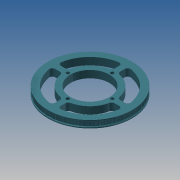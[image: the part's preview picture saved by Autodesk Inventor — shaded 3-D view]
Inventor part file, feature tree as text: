
AUTODESK INVENTOR PART (.ipt)
format: ipt  version: 2013 (Build 170138000, 138)  size: 1,232,896 bytes
history: native  units: mm
features: extrude x7, sketch x7, pattern_circular x3, mirror x1, chamfer x1, fillet x1
ambient origin geometry x8: Origin, YZ Plane, XZ Plane, XY Plane, X Axis, Y Axis, Z Axis, Center Point
bodies: Solid2 (feature_tree)
feature tree (20):
  extrude  "Extrusion11"  Depth=10.0mm
  extrude  "Extrusion12"  Depth=3.5mm
  pattern_circular  "Circular Pattern4"  Count=235  [1 undecoded]
  extrude  "Extrusion16"  Depth=1.0mm
  mirror  "Mirror2"
  chamfer  "Chamfer3"  Distance=2.5mm
  extrude  "Extrusion17"  Depth=1.0mm TaperAngle=45.0deg
  extrude  "Extrusion8"  Depth=12.0mm
  pattern_circular  "Circular Pattern5"  Count=7  [1 undecoded]
  fillet  "Fillet2"  Radius=10.0mm
  extrude  "Extrusion18"  Depth=2.5mm TaperAngle=0.0deg
  extrude  "Extrusion19"  Depth=40.0mm TaperAngle=360.0deg
  pattern_circular  "Circular Pattern6"  [2 undecoded]
  sketch  "Sketch8"  dims[d11=0.254mm d60=10.0mm]
  sketch  "Sketch9"  dims[d62=10.0mm d63=0.0mm d69=3.5mm]
  sketch  "Sketch11"  dims[d78=149.097647mm]
  sketch  "Sketch12"  dims[d80=8.0mm d81=0.0mm]
  sketch  "Sketch13"  dims[d82=1.59mm]
  sketch  "Sketch14"  dims[d84=8.0mm d85=0.0mm d86=2350.0mm]
  sketch  "Sketch15"  dims[d87=360.0deg d96=1.0mm d97=2.5mm d98=0.0mm d99=1.0mm d100=2.0mm d101=45.0deg d102=12.0mm d103=70.0mm d104=10.0mm d105=2.5mm d106=0.0mm d107=40.0mm d108=360.0deg d110=5.0mm d111=40.0mm d112=2.5mm d113=0.0mm d114=5.5mm d115=4.0mm d116=0.0mm d117=40.0mm d118=360.0deg]
note: 4 required parameter values undecoded (feature->parameter linkage not recoverable at this tier; creation-order binding heuristic only, values carry confidence <= 0.55)
